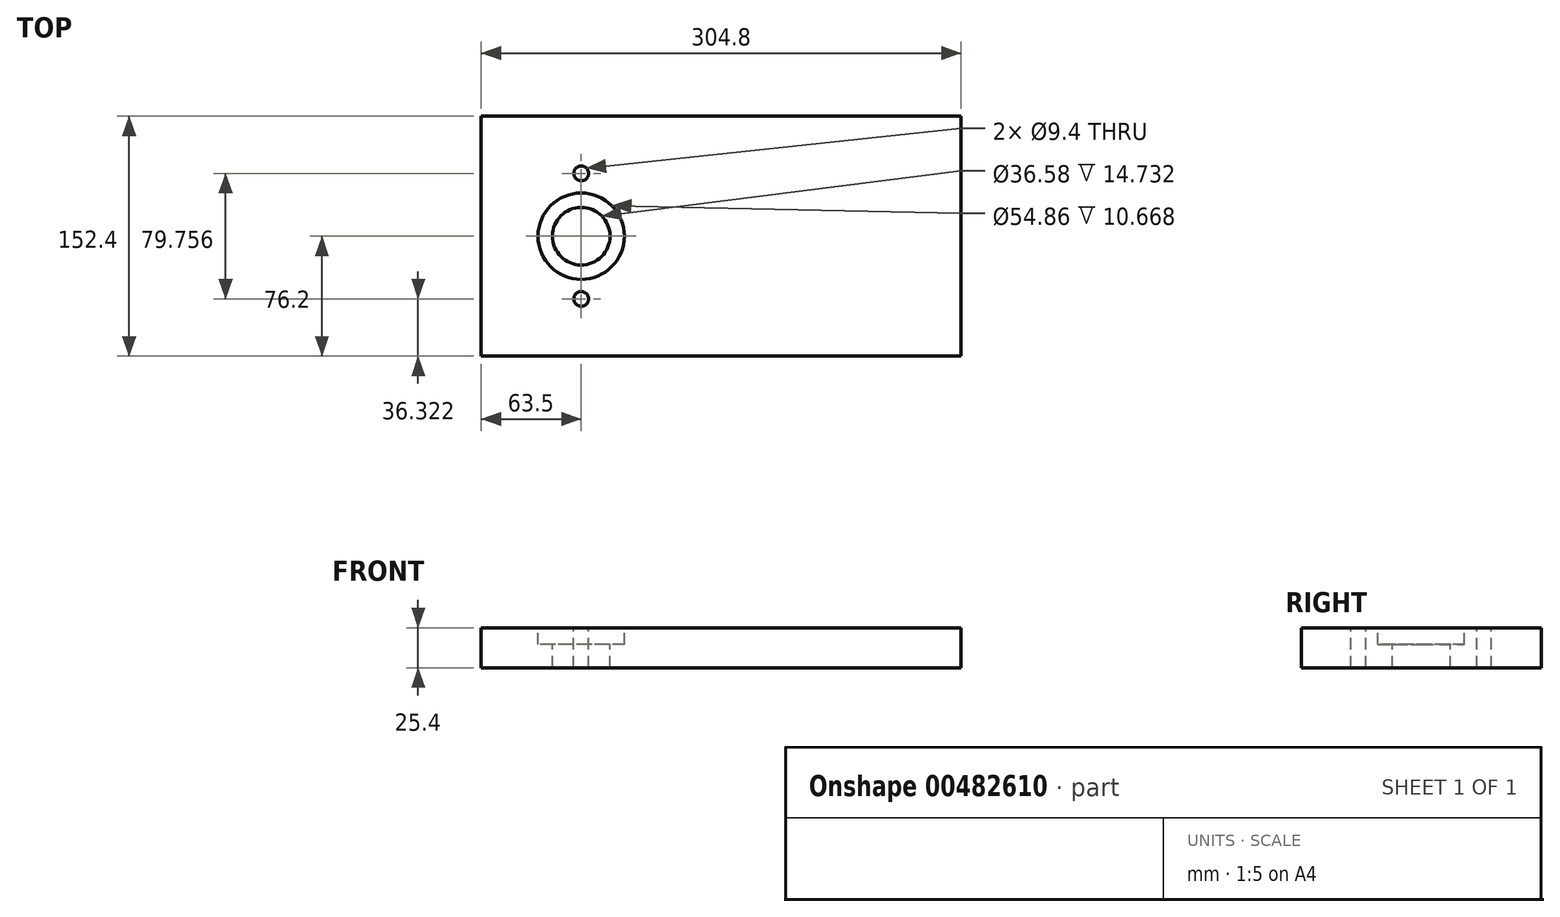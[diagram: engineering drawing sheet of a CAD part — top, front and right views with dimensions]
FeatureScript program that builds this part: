
annotation { "Feature Type Name" : "Feature", "Feature Type Description" : "" }
export const myFeature = defineFeature(function(context is Context, id is Id, definition is map)
    precondition{}
    {
        {
            var Q0;
            Q0=qCreatedBy(makeId("Top.planeOp"),FACE);
            var sketch = newSketch(context, id + "F0", { "sketchPlane" : qUnion([Q0])});
            skLineSegment(sketch, "E0.bottom", {"start": v(-152.4, 76.2) * mm, "end": v(152.4, 76.2) * mm});
            skLineSegment(sketch, "E0.top", {"start": v(-152.4, -76.2) * mm, "end": v(152.4, -76.2) * mm});
            skLineSegment(sketch, "E0.left", {"start": v(-152.4, 76.2) * mm, "end": v(-152.4, -76.2) * mm});
            skLineSegment(sketch, "E0.right", {"start": v(152.4, 76.2) * mm, "end": v(152.4, -76.2) * mm});
            skPoint(sketch, "E0.middle", {"position": v(0, 0) * mm});
            skSolve(sketch);
        }
        {
            var Q0;
            Q0=qSketchRegion(id+"F0",true);
            extrude(context, id + "F1", {"entities" : qUnion([Q0]), "oppositeDirection" : true, "depth" : 25.4 * mm});
        }
        {
            var Q0;
            Q0=makeQuery(id+"F1.opExtrude","CAP_FACE",FACE,{"disambiguationData":[OSD([sQuery(id+"F0.wireOp",EDGE,"E0.bottom"),sQuery(id+"F0.wireOp",EDGE,"E0.top"),sQuery(id+"F0.wireOp",EDGE,"E0.left"),sQuery(id+"F0.wireOp",EDGE,"E0.right")])],"isStart":true});
            var sketch = newSketch(context, id + "F2", { "sketchPlane" : qUnion([Q0])});
            skCircle(sketch, "E1", {"center": v(-88.9, 0) * mm, "radius": 18.29 * mm});
            skSolve(sketch);
        }
        {
            var Q0;
            Q0=qSketchRegion(id+"F2",true);
            extrude(context, id + "F3", {"entities" : qUnion([Q0]), "operationType" : NewBodyOperationType.REMOVE, "endBound" : BoundingType.THROUGH_ALL, "oppositeDirection" : true, "depth" : 25.4 * mm});
        }
        {
            var Q0;
            Q0=makeQuery(id+"F1.opExtrude","CAP_FACE",FACE,{"disambiguationData":[OSD([sQuery(id+"F0.wireOp",EDGE,"E0.bottom"),sQuery(id+"F0.wireOp",EDGE,"E0.top"),sQuery(id+"F0.wireOp",EDGE,"E0.left"),sQuery(id+"F0.wireOp",EDGE,"E0.right")])],"isStart":true});
            var sketch = newSketch(context, id + "F4", { "sketchPlane" : qUnion([Q0])});
            skCircle(sketch, "E2", {"center": v(-88.9, 0) * mm, "radius": 27.43 * mm});
            skSolve(sketch);
        }
        {
            var Q0;
            Q0=qSketchRegion(id+"F4",true);
            extrude(context, id + "F5", {"entities" : qUnion([Q0]), "operationType" : NewBodyOperationType.REMOVE, "oppositeDirection" : true, "depth" : 10.67 * mm});
        }
        {
            var Q0;
            Q0=makeQuery(id+"F1.opExtrude","CAP_FACE",FACE,{"disambiguationData":[OSD([sQuery(id+"F0.wireOp",EDGE,"E0.bottom"),sQuery(id+"F0.wireOp",EDGE,"E0.top"),sQuery(id+"F0.wireOp",EDGE,"E0.left"),sQuery(id+"F0.wireOp",EDGE,"E0.right")])],"isStart":true});
            var sketch = newSketch(context, id + "F6", { "sketchPlane" : qUnion([Q0])});
            skCircle(sketch, "E3", {"center": v(-88.9, 39.88) * mm, "radius": 4.7 * mm});
            skCircle(sketch, "E4", {"center": v(-88.9, -39.88) * mm, "radius": 4.7 * mm});
            skCircle(sketch, "E5", {"center": v(-88.9, 0) * mm, "radius": 39.88 * mm, "construction": true});
            skLineSegment(sketch, "E6", {"start": v(-88.9, 39.88) * mm, "end": v(-88.9, -39.88) * mm, "construction": true});
            skSolve(sketch);
        }
        {
            var Q0;
            Q0=makeQuery(id+"F6.imprint","IMPRINT",FACE,{"disambiguationData":[TD([[makeQuery(id+"F6.imprint","IMPRINT",EDGE,{"derivedFrom":sQuery(id+"F6.wireOp",EDGE,"E3")}),1.0]])]});
            var Q1;
            Q1=makeQuery(id+"F6.imprint","IMPRINT",FACE,{"disambiguationData":[TD([[makeQuery(id+"F6.imprint","IMPRINT",EDGE,{"derivedFrom":sQuery(id+"F6.wireOp",EDGE,"E4")}),1.0]])]});
            var Q2;
            Q2=sQuery(id+"F6.wireOp",EDGE,"46920e1b-e200-4218-b525-06abca21a441");
            var Q3;
            Q3=sQuery(id+"F6.wireOp",EDGE,"21X3tvqT-YTCq-JDmM-rHFV-8MgQzdfabW2A");
            extrude(context, id + "F7", {"entities" : qUnion([Q0, Q1]), "operationType" : NewBodyOperationType.REMOVE, "surfaceEntities" : qUnion([Q2, Q3]), "endBound" : BoundingType.THROUGH_ALL, "oppositeDirection" : true, "depth" : 25.4 * mm});
        }
    });
